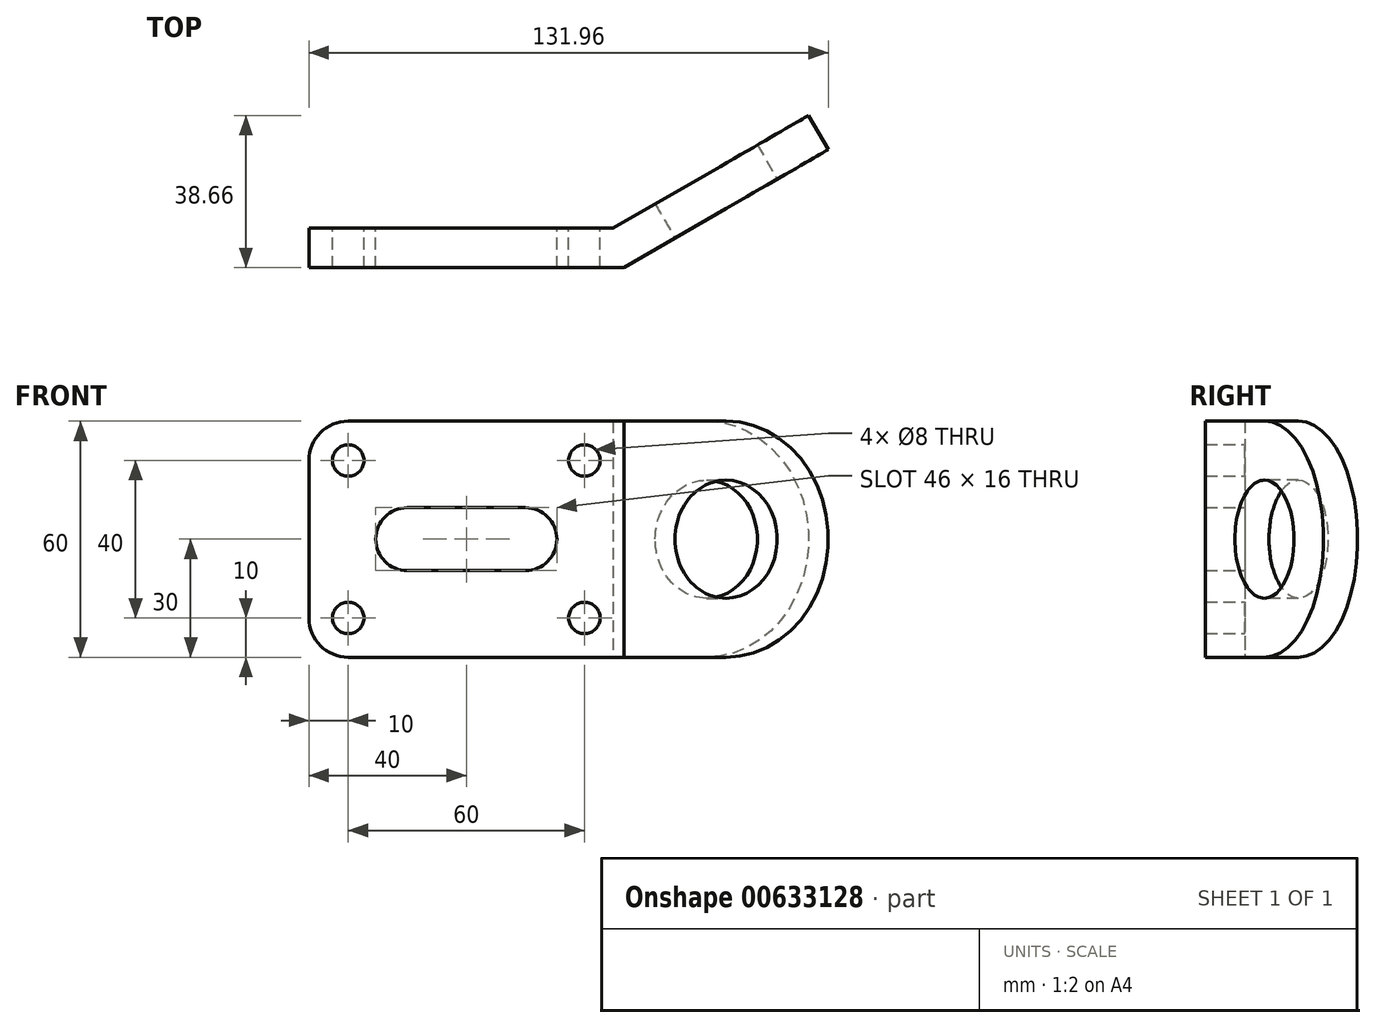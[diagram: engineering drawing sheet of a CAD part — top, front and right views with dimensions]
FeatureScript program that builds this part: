
annotation { "Feature Type Name" : "Feature", "Feature Type Description" : "" }
export const myFeature = defineFeature(function(context is Context, id is Id, definition is map)
    precondition{}
    {
        {
            var Q0;
            Q0=qCreatedBy(makeId("Front.planeOp"),FACE);
            var sketch = newSketch(context, id + "F0", { "sketchPlane" : qUnion([Q0])});
            skLineSegment(sketch, "E0", {"start": v(-30, 30) * mm, "end": v(40, 30) * mm});
            skLineSegment(sketch, "E1", {"start": v(40, 30) * mm, "end": v(40, -30) * mm});
            skLineSegment(sketch, "E2", {"start": v(40, -30) * mm, "end": v(-30, -30) * mm});
            skArc(sketch, "E3", {"start": v(-30, 30) * mm, "mid": v(-37.07, 27.07) * mm, "end": v(-40, 20) * mm});
            skArc(sketch, "E4", {"start": v(-40, -20) * mm, "mid": v(-37.07, -27.07) * mm, "end": v(-30, -30) * mm});
            skLineSegment(sketch, "E5", {"start": v(-40, 20) * mm, "end": v(-40, -20) * mm});
            skLineSegment(sketch, "E6.bottom", {"start": v(15, -8) * mm, "end": v(-15, -8) * mm});
            skLineSegment(sketch, "E6.top", {"start": v(15, 8) * mm, "end": v(-15, 8) * mm});
            skPoint(sketch, "E6.middle", {"position": v(0, 0) * mm});
            skCircle(sketch, "E7", {"center": v(-30, 20) * mm, "radius": 4 * mm});
            skCircle(sketch, "E8", {"center": v(-30, -20) * mm, "radius": 4 * mm});
            skCircle(sketch, "E9", {"center": v(30, -20) * mm, "radius": 4 * mm});
            skCircle(sketch, "E10", {"center": v(30, 20) * mm, "radius": 4 * mm});
            skArc(sketch, "E11", {"start": v(-15, 8) * mm, "mid": v(-23, 0) * mm, "end": v(-15, -8) * mm});
            skArc(sketch, "E12", {"start": v(15, -8) * mm, "mid": v(23, 0) * mm, "end": v(15, 8) * mm});
            skSolve(sketch);
        }
        {
            var Q0;
            Q0=makeQuery(id+"F0.imprint","IMPRINT",FACE,{"disambiguationData":[TD([[makeQuery(id+"F0.imprint","IMPRINT",EDGE,{"derivedFrom":sQuery(id+"F0.wireOp",EDGE,"E0")}),-1.0]])]});
            extrude(context, id + "F1", {"entities" : qUnion([Q0]), "depth" : 10 * mm, "offsetDistance" : 25.4 * mm});
        }
        {
            var Q0;
            Q0=makeQuery(id+"F1.opExtrude","CAP_EDGE",EDGE,{"disambiguationData":[OSD([sQuery(id+"F0.wireOp",EDGE,"E1")])],"isStart":false});
            cPlane(context, id + "F2", {"entities" : qUnion([Q0]), "cplaneType" : CPlaneType.LINE_ANGLE, "offset" : 25.4 * mm, "angle" : 60 * degree, "width" : 152.4 * mm, "height" : 152.4 * mm});
        }
        {
            var Q0;
            Q0=qCreatedBy(id+"F2.planeOp",FACE);
            var sketch = newSketch(context, id + "F3", { "sketchPlane" : qUnion([Q0])});
            skLineSegment(sketch, "E13", {"start": v(-29.64, -30) * mm, "end": v(-59.64, -30) * mm});
            skLineSegment(sketch, "E14", {"start": v(-29.64, 30) * mm, "end": v(-59.64, 30) * mm});
            skArc(sketch, "E15", {"start": v(-59.64, 30) * mm, "mid": v(-89.64, 0) * mm, "end": v(-59.64, -30) * mm});
            skLineSegment(sketch, "E16", {"start": v(-29.64, -30) * mm, "end": v(-29.64, 30) * mm});
            skCircle(sketch, "E17", {"center": v(-59.64, 0) * mm, "radius": 15 * mm});
            skSolve(sketch);
        }
        {
            var Q0;
            Q0=makeQuery(id+"F3.imprint","IMPRINT",FACE,{"disambiguationData":[TD([[makeQuery(id+"F3.imprint","IMPRINT",EDGE,{"derivedFrom":sQuery(id+"F3.wireOp",EDGE,"E13")}),-1.0]])]});
            extrude(context, id + "F4", {"entities" : qUnion([Q0]), "operationType" : NewBodyOperationType.ADD, "depth" : 10 * mm, "offsetDistance" : 25.4 * mm});
        }
    });
